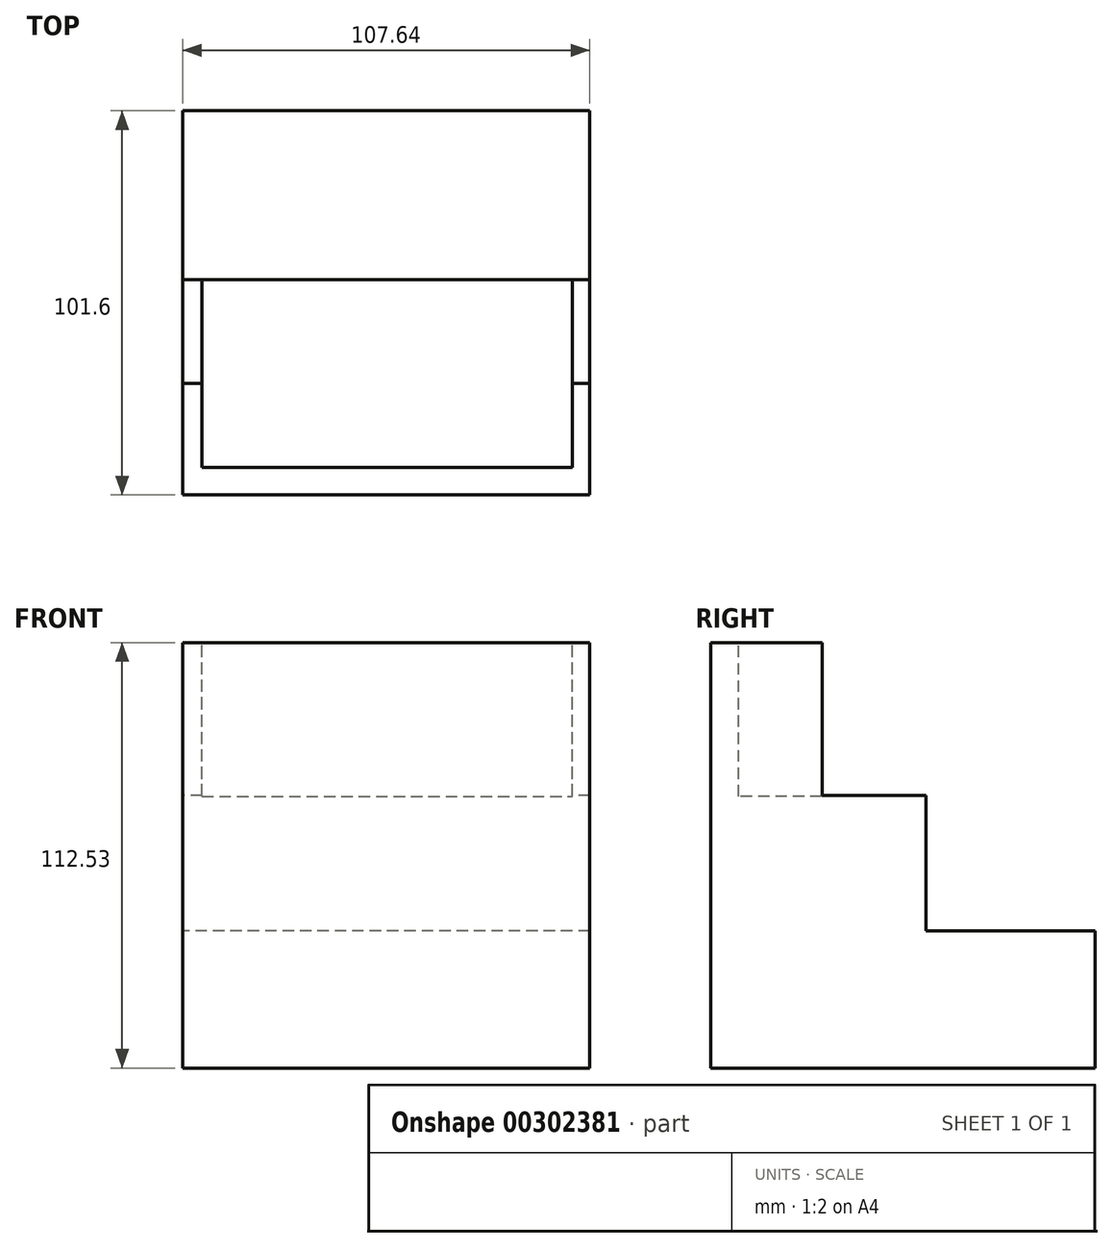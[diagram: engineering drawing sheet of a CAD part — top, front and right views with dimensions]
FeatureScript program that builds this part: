
annotation { "Feature Type Name" : "Feature", "Feature Type Description" : "" }
export const myFeature = defineFeature(function(context is Context, id is Id, definition is map)
    precondition{}
    {
        {
            var Q0;
            Q0=qCreatedBy(makeId("Front.planeOp"),FACE);
            var sketch = newSketch(context, id + "F0", { "sketchPlane" : qUnion([Q0])});
            skLineSegment(sketch, "E0.bottom", {"start": v(-55.55, 56.4) * mm, "end": v(52.1, 56.4) * mm});
            skLineSegment(sketch, "E0.top", {"start": v(-55.55, -56.12) * mm, "end": v(52.1, -56.12) * mm});
            skLineSegment(sketch, "E0.left", {"start": v(-55.55, 56.4) * mm, "end": v(-55.55, -56.12) * mm});
            skLineSegment(sketch, "E0.right", {"start": v(52.1, 56.4) * mm, "end": v(52.1, -56.12) * mm});
            skSolve(sketch);
        }
        {
            var Q0;
            Q0 = qSketchRegion(id + "F0", true);
            extrude(context, id + "F1", {"entities" : qUnion([Q0]), "depth" : 50.8 * mm, "hasSecondDirection" : true, "secondDirectionOppositeDirection" : true, "secondDirectionDepth" : 50.8 * mm});
        }
        {
            var Q0;
            Q0=makeQuery(id+"F1.opExtrude","CAP_FACE",FACE,{"disambiguationData":[OSD([sQuery(id+"F0.wireOp",EDGE,"E0.bottom"),sQuery(id+"F0.wireOp",EDGE,"E0.top"),sQuery(id+"F0.wireOp",EDGE,"E0.left"),sQuery(id+"F0.wireOp",EDGE,"E0.right")])],"isStart":true});
            var sketch = newSketch(context, id + "F2", { "sketchPlane" : qUnion([Q0])});
            skLineSegment(sketch, "E1.bottom", {"start": v(-52.1, 56.4) * mm, "end": v(55.55, 56.4) * mm});
            skLineSegment(sketch, "E1.top", {"start": v(-52.1, -19.88) * mm, "end": v(55.55, -19.88) * mm});
            skLineSegment(sketch, "E1.left", {"start": v(-52.1, 56.4) * mm, "end": v(-52.1, -19.88) * mm});
            skLineSegment(sketch, "E1.right", {"start": v(55.55, 56.4) * mm, "end": v(55.55, -19.88) * mm});
            skSolve(sketch);
        }
        {
            var Q0;
            Q0 = qSketchRegion(id + "F2", true);
            extrude(context, id + "F3", {"entities" : qUnion([Q0]), "operationType" : NewBodyOperationType.REMOVE, "oppositeDirection" : true, "depth" : 44.7 * mm});
        }
        {
            var Q0;
            Q0=makeQuery(id+"F3.boolean.opBoolean","COPY",FACE,{"derivedFrom":makeQuery(id+"F3.opExtrude","CAP_FACE",FACE,{"disambiguationData":[OSD([sQuery(id+"F2.wireOp",EDGE,"E1.bottom"),sQuery(id+"F2.wireOp",EDGE,"E1.top"),sQuery(id+"F2.wireOp",EDGE,"E1.left"),sQuery(id+"F2.wireOp",EDGE,"E1.right")])],"isStart":false})});
            var sketch = newSketch(context, id + "F4", { "sketchPlane" : qUnion([Q0])});
            skLineSegment(sketch, "E2.bottom", {"start": v(-52.1, 56.4) * mm, "end": v(55.55, 56.4) * mm});
            skLineSegment(sketch, "E2.top", {"start": v(-52.1, 15.96) * mm, "end": v(55.55, 15.96) * mm});
            skLineSegment(sketch, "E2.left", {"start": v(-52.1, 56.4) * mm, "end": v(-52.1, 15.96) * mm});
            skLineSegment(sketch, "E2.right", {"start": v(55.55, 56.4) * mm, "end": v(55.55, 15.96) * mm});
            skSolve(sketch);
        }
        {
            var Q0;
            Q0 = qSketchRegion(id + "F4", true);
            extrude(context, id + "F5", {"entities" : qUnion([Q0]), "operationType" : NewBodyOperationType.REMOVE, "oppositeDirection" : true, "depth" : 27.43 * mm});
        }
        {
            var Q0;
            Q0=qCreatedBy(makeId("Top.planeOp"),FACE);
            cPlane(context, id + "F6", {"entities" : qUnion([Q0]), "cplaneType" : CPlaneType.OFFSET, "offset" : 57.4 * mm, "width" : 152.4 * mm, "height" : 152.4 * mm});
        }
        {
            var Q0;
            Q0=qCreatedBy(id+"F6.planeOp",FACE);
            var sketch = newSketch(context, id + "F7", { "sketchPlane" : qUnion([Q0])});
            skLineSegment(sketch, "E3.bottom", {"start": v(-50.37, 45.47) * mm, "end": v(47.49, 45.47) * mm});
            skLineSegment(sketch, "E3.top", {"start": v(-50.37, -43.46) * mm, "end": v(47.49, -43.46) * mm});
            skLineSegment(sketch, "E3.left", {"start": v(-50.37, 45.47) * mm, "end": v(-50.37, -43.46) * mm});
            skLineSegment(sketch, "E3.right", {"start": v(47.49, 45.47) * mm, "end": v(47.49, -43.46) * mm});
            skSolve(sketch);
        }
        {
            var Q0;
            Q0 = qSketchRegion(id + "F7", true);
            extrude(context, id + "F8", {"entities" : qUnion([Q0]), "operationType" : NewBodyOperationType.REMOVE, "oppositeDirection" : true, "depth" : 41.66 * mm});
        }
    });
